# Revit family: svetilnik_alfresco_dtu-29-af_star
name_source: partatom
category: Lighting Fixtures
revit_build: Autodesk Revit 2016 (Build: 20150506_1715(x64)
units: mm (PartAtom-declared; Revit-internal decimal feet)

## family parameters
Always vertical = Yes
Cut with Voids When Loaded = No
Light Source = Yes
Part Type = Normal
Room Calculation Point = No
Round Connector Dimension = Use Diameter
Shared = No
Work Plane-Based = No

## types (1)
- Светодиодный светильник STAR ДТУ-29-AF-50Вт
    ADSK_Артикул = ДТУ291
    ADSK_Единица измерения = шт
    ADSK_Классификация нагрузок = Освещение
    ADSK_Количество фаз = 2
    ADSK_Количество фаз числовое = 2
    ADSK_Коэффициент мощности = 0.97
    ADSK_Масса = 56
    ADSK_Модель = Стрит-Премьер ДТУ-34-AF
    ADSK_Наименование = Светодиодный светильник STAR ДТУ-29-AF-50Вт-4,5
    ADSK_Напряжение = 220 V
    ADSK_Номинальная мощность = 50 W
    ADSK_Полная мощность = 52 VA
    ADSK_Размер_Высота = 4500 mm
    ADSK_Размер_Длина = 219 mm  [stored 0.718504 ft]
    ADSK_Размер_Ширина = 219 mm  [stored 0.718504 ft]
    ADSK_Ток = 0 A
    ADSK_Энергоэффективность = 120 lm/W
    Apparent Load = 52 VA
    Color Filter = 16777215
    Dimming Lamp Color Temperature Shift = <None>
    Emit Shape Visible in Rendering = No
    Emit from Circle Diameter = 219 mm  [stored 0.718504 ft]
    IP Class = IP 65
    Manufacturer = ALFRESCO
    Photometric Web File = Star 40w.ies
    Tilt Angle = 90.00°
    URL = http://www.allfresco.ru
    Блок аварийного питания = No
    Высота нижней части = 1600 mm  [stored 5.24934 ft]
    Высота средней части = 2616 mm
    Класс Защиты = 1
    Класс пожароопасности = F (светильники предназначены для установки непосредственно на поверхность из нормально воспламеняемых матеоиалов)
    Климатическая зона = У1
    Материал опоры = Сталь, окрашенная, черная
    Область использования = Ландшафт, коттедж.поселки,микрорайоны
    Световой поток = 4800 lm
    Сечение по фланцу = 300 mm
    Температура эксплуатации = -35 +40
    Тип ИС = LED-СОВ
    Тип КСС = Sym
    Тип ПРА = -
    Тип продукции = LED-СОВ
    Цветовая температура = 3000-5500

note: [stored X ft] marks values corroborated as IEEE doubles in the binary element streams (Revit-internal decimal feet)
